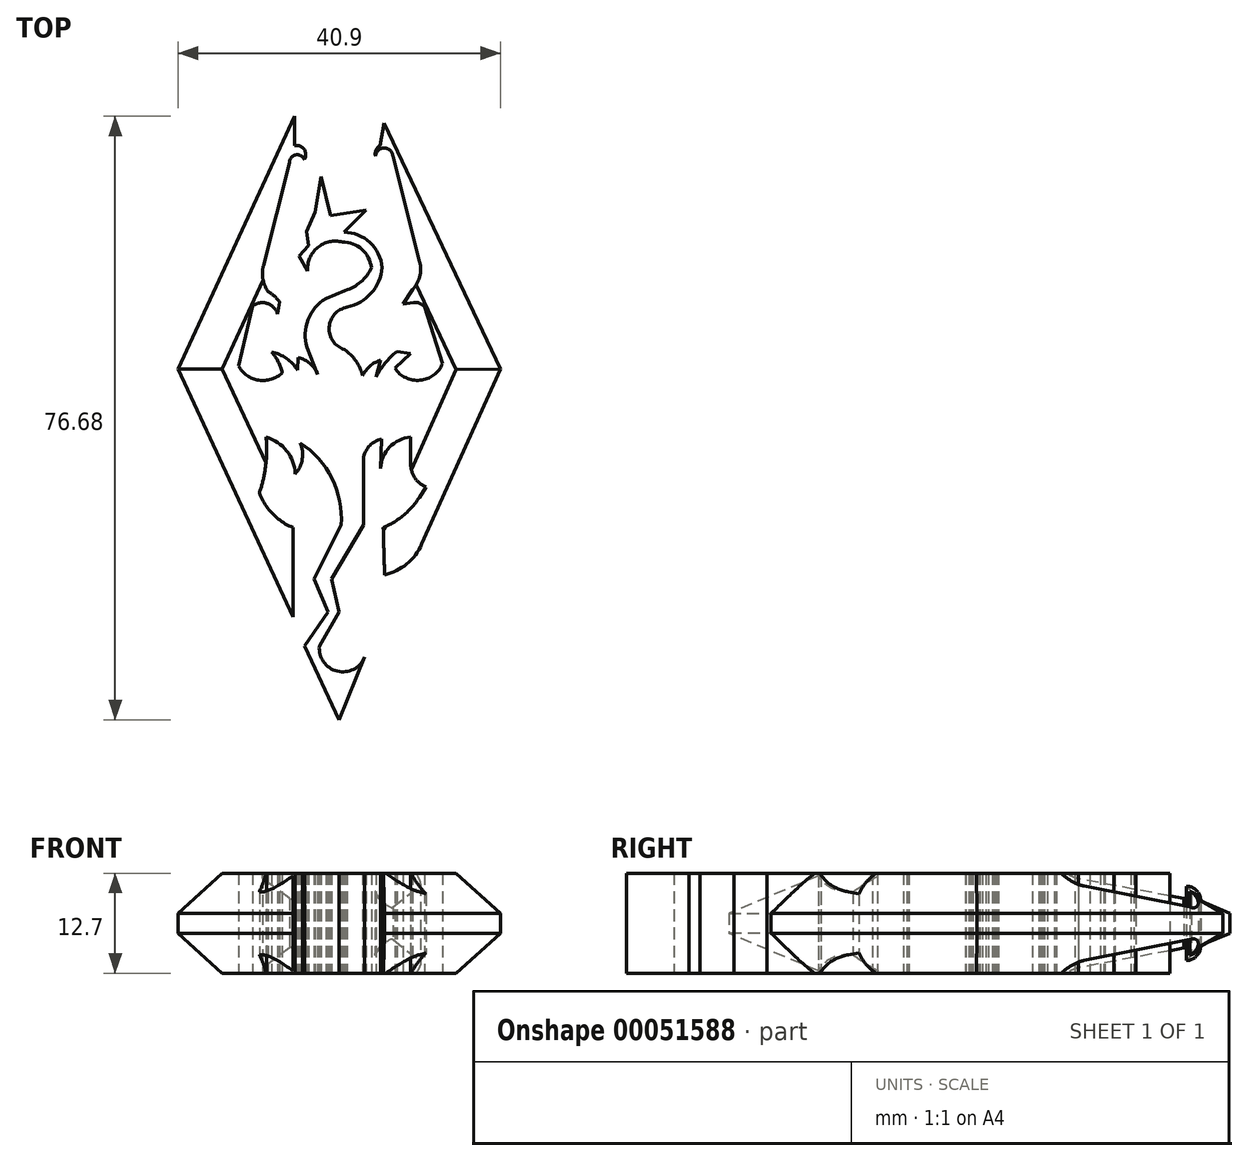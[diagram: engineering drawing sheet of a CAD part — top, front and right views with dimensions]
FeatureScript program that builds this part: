
annotation { "Feature Type Name" : "Feature", "Feature Type Description" : "" }
export const myFeature = defineFeature(function(context is Context, id is Id, definition is map)
    precondition{}
    {
        {
            var Q0;
            Q0=qCreatedBy(makeId("Top.planeOp"),FACE);
            var sketch = newSketch(context, id + "F0", { "sketchPlane" : qUnion([Q0])});
            skPoint(sketch, "E0", {"position": v(18.78, 44.56) * mm});
            skPoint(sketch, "E1", {"position": v(59.68, 44.56) * mm});
            skPoint(sketch, "E2", {"position": v(44.98, 18.41) * mm});
            skPoint(sketch, "E3", {"position": v(49.7, 22.32) * mm});
            skPoint(sketch, "E4", {"position": v(44.81, 24.42) * mm});
            skPoint(sketch, "E5", {"position": v(33.36, 24.42) * mm});
            skPoint(sketch, "E6", {"position": v(33.36, 13.06) * mm});
            skPoint(sketch, "E7", {"position": v(29.07, 28.81) * mm});
            skPoint(sketch, "E8", {"position": v(29.94, 35.9) * mm});
            skPoint(sketch, "E9", {"position": v(33.64, 31.25) * mm});
            skPoint(sketch, "E10", {"position": v(34.27, 35.19) * mm});
            skPoint(sketch, "E11", {"position": v(39.46, 24.72) * mm});
            skPoint(sketch, "E12", {"position": v(36, 17.88) * mm});
            skPoint(sketch, "E13", {"position": v(38.28, 17.88) * mm});
            skPoint(sketch, "E14", {"position": v(42.3, 24.72) * mm});
            skPoint(sketch, "E15", {"position": v(37.8, 13.7) * mm});
            skPoint(sketch, "E16", {"position": v(39.22, 13.7) * mm});
            skPoint(sketch, "E17", {"position": v(36.7, 9.38) * mm});
            skPoint(sketch, "E18", {"position": v(34.82, 9.38) * mm});
            skPoint(sketch, "E19", {"position": v(42.45, 7.96) * mm});
            skPoint(sketch, "E20", {"position": v(39.22, 0) * mm});
            skPoint(sketch, "E21", {"position": v(44.63, 35.67) * mm});
            skPoint(sketch, "E22", {"position": v(42.28, 32.86) * mm});
            skPoint(sketch, "E23", {"position": v(44.47, 31.92) * mm});
            skPoint(sketch, "E24", {"position": v(48.3, 35.9) * mm});
            skPoint(sketch, "E25", {"position": v(48.3, 32.47) * mm});
            skPoint(sketch, "E26", {"position": v(50.25, 29.58) * mm});
            skPoint(sketch, "E27", {"position": v(49.4, 28.25) * mm});
            skLineSegment(sketch, "E28", {"start": v(42.3, 24.72) * mm, "end": v(42.28, 32.86) * mm});
            skLineSegment(sketch, "E29", {"start": v(44.47, 31.92) * mm, "end": v(44.63, 35.67) * mm});
            skLineSegment(sketch, "E30", {"start": v(48.3, 35.9) * mm, "end": v(48.3, 32.47) * mm});
            skLineSegment(sketch, "E31", {"start": v(50.25, 29.58) * mm, "end": v(49.4, 28.25) * mm});
            skLineSegment(sketch, "E32", {"start": v(59.68, 44.56) * mm, "end": v(49.7, 22.32) * mm});
            skLineSegment(sketch, "E33", {"start": v(18.78, 44.56) * mm, "end": v(33.36, 13.06) * mm});
            skLineSegment(sketch, "E34", {"start": v(33.36, 24.42) * mm, "end": v(33.36, 13.06) * mm});
            skLineSegment(sketch, "E35", {"start": v(39.46, 24.72) * mm, "end": v(36, 17.88) * mm});
            skLineSegment(sketch, "E36", {"start": v(37.8, 13.7) * mm, "end": v(36, 17.88) * mm});
            skLineSegment(sketch, "E37", {"start": v(37.8, 13.7) * mm, "end": v(34.82, 9.38) * mm});
            skLineSegment(sketch, "E38", {"start": v(34.82, 9.38) * mm, "end": v(39.22, 0) * mm});
            skLineSegment(sketch, "E39", {"start": v(42.45, 7.96) * mm, "end": v(39.22, 0) * mm});
            skArc(sketch, "E40", {"start": v(36.7, 9.38) * mm, "mid": v(38.96, 6.18) * mm, "end": v(42.45, 7.96) * mm});
            skLineSegment(sketch, "E41", {"start": v(42.3, 24.72) * mm, "end": v(38.28, 17.88) * mm});
            skLineSegment(sketch, "E42", {"start": v(39.22, 13.7) * mm, "end": v(38.28, 17.88) * mm});
            skLineSegment(sketch, "E43", {"start": v(36.7, 9.38) * mm, "end": v(39.22, 13.7) * mm});
            skArc(sketch, "E44", {"start": v(39.46, 24.72) * mm, "mid": v(38.28, 30.66) * mm, "end": v(34.27, 35.19) * mm});
            skArc(sketch, "E45", {"start": v(33.64, 31.25) * mm, "mid": v(34.52, 33.13) * mm, "end": v(34.27, 35.19) * mm});
            skArc(sketch, "E46", {"start": v(33.64, 31.25) * mm, "mid": v(32.55, 34.18) * mm, "end": v(29.94, 35.9) * mm});
            skArc(sketch, "E47", {"start": v(29.07, 28.81) * mm, "mid": v(29.88, 32.3) * mm, "end": v(29.94, 35.9) * mm});
            skArc(sketch, "E48", {"start": v(29.07, 28.81) * mm, "mid": v(30.75, 26.17) * mm, "end": v(33.36, 24.42) * mm});
            skArc(sketch, "E49", {"start": v(44.63, 35.67) * mm, "mid": v(42.94, 34.7) * mm, "end": v(42.28, 32.86) * mm});
            skArc(sketch, "E50", {"start": v(48.3, 35.9) * mm, "mid": v(45.63, 34.64) * mm, "end": v(44.47, 31.92) * mm});
            skArc(sketch, "E51", {"start": v(48.3, 32.47) * mm, "mid": v(48.83, 30.72) * mm, "end": v(50.25, 29.58) * mm});
            skArc(sketch, "E52", {"start": v(44.81, 24.42) * mm, "mid": v(47.4, 25.99) * mm, "end": v(49.4, 28.25) * mm});
            skArc(sketch, "E53", {"start": v(44.98, 18.41) * mm, "mid": v(47.8, 19.82) * mm, "end": v(49.7, 22.32) * mm});
            skLineSegment(sketch, "E54", {"start": v(44.81, 24.42) * mm, "end": v(44.98, 18.41) * mm});
            skPoint(sketch, "E55", {"position": v(33.55, 76.68) * mm});
            skPoint(sketch, "E56", {"position": v(44.93, 75.78) * mm});
            skLineSegment(sketch, "E57", {"start": v(33.55, 76.68) * mm, "end": v(18.78, 44.56) * mm});
            skLineSegment(sketch, "E58", {"start": v(44.93, 75.78) * mm, "end": v(59.68, 44.56) * mm});
            skLineSegment(sketch, "E59", {"start": v(33.55, 76.68) * mm, "end": v(33.55, 72.95) * mm});
            skPoint(sketch, "E60", {"position": v(44.42, 72.95) * mm});
            skPoint(sketch, "E61", {"position": v(43.82, 71.58) * mm});
            skPoint(sketch, "E62", {"position": v(34.8, 71.16) * mm});
            skPoint(sketch, "E63", {"position": v(32.92, 70.82) * mm});
            skPoint(sketch, "E64", {"position": v(29.6, 57.7) * mm});
            skPoint(sketch, "E65", {"position": v(30.2, 54.37) * mm});
            skPoint(sketch, "E66", {"position": v(31.64, 53.1) * mm});
            skPoint(sketch, "E67", {"position": v(31.38, 51.56) * mm});
            skPoint(sketch, "E68", {"position": v(28.23, 52.58) * mm});
            skPoint(sketch, "E69", {"position": v(26.44, 44.92) * mm});
            skPoint(sketch, "E70", {"position": v(31.98, 44.07) * mm});
            skPoint(sketch, "E71", {"position": v(30.62, 46.7) * mm});
            skPoint(sketch, "E72", {"position": v(33.94, 44.4) * mm});
            skPoint(sketch, "E73", {"position": v(34.02, 46.02) * mm});
            skPoint(sketch, "E74", {"position": v(36.5, 43.9) * mm});
            skPoint(sketch, "E75", {"position": v(35.13, 47.3) * mm});
            skPoint(sketch, "E76", {"position": v(37.52, 53.52) * mm});
            skArc(sketch, "E77", {"start": v(34.8, 71.16) * mm, "mid": v(34.77, 72.46) * mm, "end": v(33.55, 72.95) * mm});
            skArc(sketch, "E78", {"start": v(44.42, 72.95) * mm, "mid": v(43.88, 72.37) * mm, "end": v(43.82, 71.58) * mm});
            skArc(sketch, "E79", {"start": v(46.04, 71.58) * mm, "mid": v(44.93, 72.66) * mm, "end": v(43.82, 71.58) * mm});
            skArc(sketch, "E80", {"start": v(34.8, 71.16) * mm, "mid": v(33.7, 71.78) * mm, "end": v(32.92, 70.82) * mm});
            skLineSegment(sketch, "E81", {"start": v(32.92, 70.82) * mm, "end": v(29.6, 57.7) * mm});
            skArc(sketch, "E82", {"start": v(29.6, 57.7) * mm, "mid": v(29.53, 55.97) * mm, "end": v(30.2, 54.37) * mm});
            skArc(sketch, "E83", {"start": v(31.64, 53.1) * mm, "mid": v(30.99, 53.82) * mm, "end": v(30.2, 54.37) * mm});
            skLineSegment(sketch, "E84", {"start": v(31.38, 51.56) * mm, "end": v(31.64, 53.1) * mm});
            skPoint(sketch, "E85", {"position": v(49.44, 58.12) * mm});
            skPoint(sketch, "E86", {"position": v(48.5, 54.63) * mm});
            skPoint(sketch, "E87", {"position": v(47.31, 52.84) * mm});
            skPoint(sketch, "E88", {"position": v(48.68, 53.01) * mm});
            skPoint(sketch, "E89", {"position": v(50.04, 52.5) * mm});
            skPoint(sketch, "E90", {"position": v(52.34, 45.26) * mm});
            skPoint(sketch, "E91", {"position": v(46.3, 44.66) * mm});
            skPoint(sketch, "E92", {"position": v(48.25, 46.54) * mm});
            skPoint(sketch, "E93", {"position": v(46.55, 46.8) * mm});
            skPoint(sketch, "E94", {"position": v(43.9, 43.55) * mm});
            skPoint(sketch, "E95", {"position": v(44.5, 45.68) * mm});
            skPoint(sketch, "E96", {"position": v(42.2, 43.72) * mm});
            skPoint(sketch, "E97", {"position": v(39.9, 47.05) * mm});
            skPoint(sketch, "E98", {"position": v(40.24, 52.41) * mm});
            skPoint(sketch, "E99", {"position": v(39.99, 54.54) * mm});
            skPoint(sketch, "E100", {"position": v(39.65, 60.68) * mm});
            skPoint(sketch, "E101", {"position": v(39.82, 61.96) * mm});
            skPoint(sketch, "E102", {"position": v(44.67, 57.44) * mm});
            skPoint(sketch, "E103", {"position": v(43.31, 57.44) * mm});
            skPoint(sketch, "E104", {"position": v(42.63, 64.77) * mm});
            skPoint(sketch, "E105", {"position": v(36.92, 69.03) * mm});
            skPoint(sketch, "E106", {"position": v(36.15, 64.51) * mm});
            skPoint(sketch, "E107", {"position": v(35.05, 62.04) * mm});
            skPoint(sketch, "E108", {"position": v(35.3, 60.25) * mm});
            skPoint(sketch, "E109", {"position": v(34.1, 58.89) * mm});
            skPoint(sketch, "E110", {"position": v(35.22, 57.01) * mm});
            skPoint(sketch, "E111", {"position": v(38.11, 64.09) * mm});
            skArc(sketch, "E112", {"start": v(39.65, 60.68) * mm, "mid": v(36.48, 60) * mm, "end": v(35.22, 57.01) * mm});
            skLineSegment(sketch, "E113", {"start": v(35.22, 57.01) * mm, "end": v(34.1, 58.89) * mm});
            skLineSegment(sketch, "E114", {"start": v(35.3, 60.25) * mm, "end": v(34.1, 58.89) * mm});
            skLineSegment(sketch, "E115", {"start": v(35.05, 62.04) * mm, "end": v(35.3, 60.25) * mm});
            skLineSegment(sketch, "E116", {"start": v(36.15, 64.51) * mm, "end": v(35.05, 62.04) * mm});
            skLineSegment(sketch, "E117", {"start": v(36.92, 69.03) * mm, "end": v(36.15, 64.51) * mm});
            skLineSegment(sketch, "E118", {"start": v(36.92, 69.03) * mm, "end": v(38.11, 64.09) * mm});
            skLineSegment(sketch, "E119", {"start": v(42.63, 64.77) * mm, "end": v(38.11, 64.09) * mm});
            skLineSegment(sketch, "E120", {"start": v(42.63, 64.77) * mm, "end": v(39.82, 61.96) * mm});
            skArc(sketch, "E121", {"start": v(44.67, 57.44) * mm, "mid": v(43.11, 60.63) * mm, "end": v(39.82, 61.96) * mm});
            skArc(sketch, "E122", {"start": v(43.31, 57.44) * mm, "mid": v(42.1, 59.76) * mm, "end": v(39.65, 60.68) * mm});
            skArc(sketch, "E123", {"start": v(39.99, 54.54) * mm, "mid": v(41.96, 55.63) * mm, "end": v(43.31, 57.44) * mm});
            skArc(sketch, "E124", {"start": v(40.24, 52.41) * mm, "mid": v(43.28, 54.2) * mm, "end": v(44.67, 57.44) * mm});
            skArc(sketch, "E125", {"start": v(40.24, 52.41) * mm, "mid": v(37.94, 49.87) * mm, "end": v(39.9, 47.05) * mm});
            skArc(sketch, "E126", {"start": v(37.52, 53.52) * mm, "mid": v(35.26, 50.82) * mm, "end": v(35.13, 47.3) * mm});
            skLineSegment(sketch, "E127", {"start": v(39.99, 54.54) * mm, "end": v(37.52, 53.52) * mm});
            skLineSegment(sketch, "E128", {"start": v(35.13, 47.3) * mm, "end": v(36.5, 43.9) * mm});
            skArc(sketch, "E129", {"start": v(42.2, 43.72) * mm, "mid": v(41.34, 45.58) * mm, "end": v(39.9, 47.05) * mm});
            skArc(sketch, "E130", {"start": v(36.5, 43.9) * mm, "mid": v(35.52, 45.26) * mm, "end": v(34.02, 46.02) * mm});
            skArc(sketch, "E131", {"start": v(33.94, 44.4) * mm, "mid": v(32.53, 45.91) * mm, "end": v(30.62, 46.7) * mm});
            skArc(sketch, "E132", {"start": v(26.44, 44.92) * mm, "mid": v(29, 43.14) * mm, "end": v(31.98, 44.07) * mm});
            skArc(sketch, "E133", {"start": v(46.3, 44.66) * mm, "mid": v(49.5, 43.13) * mm, "end": v(52.34, 45.26) * mm});
            skArc(sketch, "E134", {"start": v(46.55, 46.8) * mm, "mid": v(45.05, 45.32) * mm, "end": v(43.9, 43.55) * mm});
            skArc(sketch, "E135", {"start": v(44.5, 45.68) * mm, "mid": v(43.14, 44.95) * mm, "end": v(42.2, 43.72) * mm});
            skLineSegment(sketch, "E136", {"start": v(44.5, 45.68) * mm, "end": v(43.9, 43.55) * mm});
            skLineSegment(sketch, "E137", {"start": v(46.55, 46.8) * mm, "end": v(48.25, 46.54) * mm});
            skLineSegment(sketch, "E138", {"start": v(46.3, 44.66) * mm, "end": v(48.25, 46.54) * mm});
            skLineSegment(sketch, "E139", {"start": v(34.02, 46.02) * mm, "end": v(33.94, 44.4) * mm});
            skArc(sketch, "E140", {"start": v(31.98, 44.07) * mm, "mid": v(31.48, 45.48) * mm, "end": v(30.62, 46.7) * mm});
            skLineSegment(sketch, "E141", {"start": v(28.23, 52.58) * mm, "end": v(26.44, 44.92) * mm});
            skArc(sketch, "E142", {"start": v(31.38, 51.56) * mm, "mid": v(30.08, 52.9) * mm, "end": v(28.23, 52.58) * mm});
            skLineSegment(sketch, "E143", {"start": v(46.04, 71.58) * mm, "end": v(49.44, 58.12) * mm});
            skLineSegment(sketch, "E144", {"start": v(44.93, 75.78) * mm, "end": v(44.42, 72.95) * mm});
            skLineSegment(sketch, "E145", {"start": v(47.31, 52.84) * mm, "end": v(48.68, 53.01) * mm});
            skLineSegment(sketch, "E146", {"start": v(48.5, 54.63) * mm, "end": v(47.31, 52.84) * mm});
            skArc(sketch, "E147", {"start": v(48.5, 54.63) * mm, "mid": v(49.43, 56.25) * mm, "end": v(49.44, 58.12) * mm});
            skArc(sketch, "E148", {"start": v(50.04, 52.5) * mm, "mid": v(49.42, 52.92) * mm, "end": v(48.68, 53.01) * mm});
            skLineSegment(sketch, "E149", {"start": v(50.04, 52.5) * mm, "end": v(52.34, 45.26) * mm});
            skSolve(sketch);
        }
        {
            var Q0;
            Q0 = qSketchRegion(id + "F0", true);
            extrude(context, id + "F1", {"entities" : qUnion([Q0]), "depth" : 12.7 * mm});
        }
        {
            var Q0;
            Q0=makeQuery(id+"F1.opExtrude","CAP_EDGE",EDGE,{"disambiguationData":[OSD([sQuery(id+"F0.wireOp",EDGE,"E57")])],"isStart":false});
            var Q1;
            Q1=makeQuery(id+"F1.opExtrude","CAP_EDGE",EDGE,{"disambiguationData":[OSD([sQuery(id+"F0.wireOp",EDGE,"E33")])],"isStart":false});
            var Q2;
            Q2=makeQuery(id+"F1.opExtrude","CAP_EDGE",EDGE,{"disambiguationData":[OSD([sQuery(id+"F0.wireOp",EDGE,"E58")])],"isStart":false});
            var Q3;
            Q3=makeQuery(id+"F1.opExtrude","CAP_EDGE",EDGE,{"disambiguationData":[OSD([sQuery(id+"F0.wireOp",EDGE,"E32")])],"isStart":false});
            var Q4;
            Q4=makeQuery(id+"F1.opExtrude","CAP_EDGE",EDGE,{"disambiguationData":[OSD([sQuery(id+"F0.wireOp",EDGE,"E53")])],"isStart":false});
            var Q5;
            Q5=makeQuery(id+"F1.opExtrude","CAP_EDGE",EDGE,{"disambiguationData":[OSD([sQuery(id+"F0.wireOp",EDGE,"E57")])],"isStart":true});
            var Q6;
            Q6=makeQuery(id+"F1.opExtrude","CAP_EDGE",EDGE,{"disambiguationData":[OSD([sQuery(id+"F0.wireOp",EDGE,"E33")])],"isStart":true});
            var Q7;
            Q7=makeQuery(id+"F1.opExtrude","CAP_EDGE",EDGE,{"disambiguationData":[OSD([sQuery(id+"F0.wireOp",EDGE,"E58")])],"isStart":true});
            var Q8;
            Q8=makeQuery(id+"F1.opExtrude","CAP_EDGE",EDGE,{"disambiguationData":[OSD([sQuery(id+"F0.wireOp",EDGE,"E32")])],"isStart":true});
            var Q9;
            Q9=makeQuery(id+"F1.opExtrude","CAP_EDGE",EDGE,{"disambiguationData":[OSD([sQuery(id+"F0.wireOp",EDGE,"E53")])],"isStart":true});
            chamfer(context, id + "F2", {"entities" : qUnion([Q0, Q1, Q2, Q3, Q4, Q5, Q6, Q7, Q8, Q9]), "width" : 5.08 * mm, "tangentPropagation" : true});
        }
    });
